# Revit family: VSB_Bollard
name_source: partatom
category: Lighting Fixtures
revit_build: Autodesk Revit 2013 (Build: 20130531_2115(x64)
units: mm (PartAtom-declared; Revit-internal decimal feet)

## types (1)
- VSB
    Apparent Load = 0 VA
    Assembly Code = D5020200
    Color Filter = 16777215
    Depth = 0' - 8"
    Description = Low Level Luminaire
    Dimming Lamp Color Temperature Shift = <None>
    Finish = Powder Coat-Kim-Dark Bronze
    Glass = Glass-KIM-Temper Molded
    Height = 3' - 7"
    Lamp = LED
    Load Classification = Lighting
    Manufacturer = Kim Lighting
    Manufacturer Fax = 626-369-2695
    MasterFormat Title = Landscape Lighting, Site Lighting, Walkway Lighting
    Model = VSB Bollard
    Note Text = LF
    Note Visible = Yes
    Number of Poles = 1
    Photometric Notes = More IES files download on Photometric Web Link
    Photometric Web File = vsb1-10l3k.ies
    Photometric Web Link = http://www.kimlighting.com
    Power Factor = 1
    Product Documentation Link = http://www.kimlighting.com
    Product Page URL = http://www.kimlighting.com
    Revisions Date = 11/02/2017
    Series = Vandal-Resistant Bollards
    Tilt Angle = 90.00°
    Type Comments = Lighted Bollard
    URL = www.kimlighting.com/
    Voltage = 120 V
    Wattage Comments = default

## geometry (parser evidence)
native form markers: Blend x1, Sweep x1
no freeform markers — native parametric forms only
